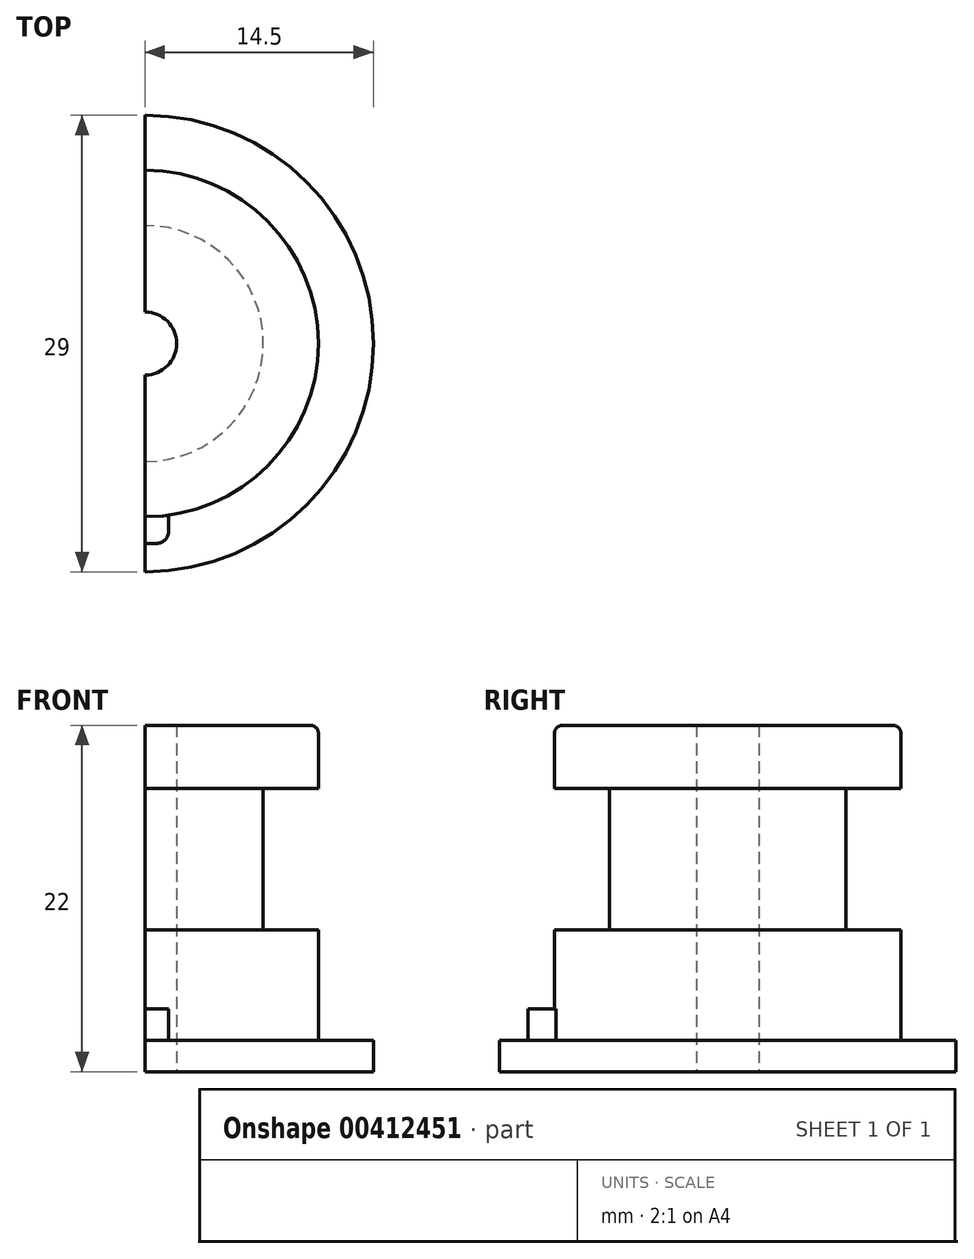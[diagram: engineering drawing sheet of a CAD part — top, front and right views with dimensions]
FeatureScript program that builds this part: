
annotation { "Feature Type Name" : "Feature", "Feature Type Description" : "" }
export const myFeature = defineFeature(function(context is Context, id is Id, definition is map)
    precondition{}
    {
        {
            var Q0;
            Q0=qCreatedBy(makeId("Top.planeOp"),FACE);
            var sketch = newSketch(context, id + "F0", { "sketchPlane" : qUnion([Q0])});
            skCircle(sketch, "E0", {"center": v(0, 0) * mm, "radius": 14.5 * mm});
            skSolve(sketch);
        }
        {
            var Q0;
            Q0=qSketchRegion(id+"F0",true);
            extrude(context, id + "F1", {"entities" : qUnion([Q0]), "depth" : 2 * mm});
        }
        {
            var Q0;
            Q0=makeQuery(id+"F1.opExtrude","CAP_FACE",FACE,{"disambiguationData":[OSD([sQuery(id+"F0.wireOp",EDGE,"E0")])],"isStart":false});
            var sketch = newSketch(context, id + "F2", { "sketchPlane" : qUnion([Q0])});
            skCircle(sketch, "E1", {"center": v(0, 0) * mm, "radius": 11 * mm});
            skSolve(sketch);
        }
        {
            var Q0;
            Q0=qSketchRegion(id+"F2",true);
            extrude(context, id + "F3", {"entities" : qUnion([Q0]), "operationType" : NewBodyOperationType.ADD, "depth" : 20 * mm});
        }
        {
            var Q0;
            Q0=makeQuery(id+"F1.opExtrude","CAP_FACE",FACE,{"disambiguationData":[OSD([sQuery(id+"F0.wireOp",EDGE,"E0")])],"isStart":true});
            var sketch = newSketch(context, id + "F4", { "sketchPlane" : qUnion([Q0])});
            skCircle(sketch, "E2", {"center": v(0, 0) * mm, "radius": 2 * mm});
            skSolve(sketch);
        }
        {
            var Q0;
            Q0=qSketchRegion(id+"F4",true);
            extrude(context, id + "F5", {"entities" : qUnion([Q0]), "operationType" : NewBodyOperationType.REMOVE, "endBound" : BoundingType.THROUGH_ALL, "oppositeDirection" : true, "depth" : 25 * mm});
        }
        {
            var Q0;
            Q0=makeQuery(id+"F1.opExtrude","CAP_FACE",FACE,{"disambiguationData":[OSD([sQuery(id+"F0.wireOp",EDGE,"E0")])],"isStart":false});
            var sketch = newSketch(context, id + "F6", { "sketchPlane" : qUnion([Q0])});
            skLineSegment(sketch, "E3.bottom", {"start": v(-1.5, -9.3) * mm, "end": v(1.5, -9.3) * mm});
            skLineSegment(sketch, "E3.top", {"start": v(-1.5, -12.7) * mm, "end": v(1.5, -12.7) * mm});
            skLineSegment(sketch, "E3.left", {"start": v(-1.5, -9.3) * mm, "end": v(-1.5, -12.7) * mm});
            skLineSegment(sketch, "E3.right", {"start": v(1.5, -9.3) * mm, "end": v(1.5, -12.7) * mm});
            skPoint(sketch, "E3.middle", {"position": v(0, -11) * mm});
            skSolve(sketch);
        }
        {
            var Q0;
            {var subQ0=sQuery(id+"F6.wireOp",EDGE,"E3.top");Q0=makeQuery(id+"F6.imprint","IMPRINT",FACE,{"disambiguationData":[TD([[makeQuery(id+"F6.imprint","IMPRINT",EDGE,{"derivedFrom":subQ0}),1.0]])]});}
            extrude(context, id + "F7", {"entities" : qUnion([Q0]), "operationType" : NewBodyOperationType.ADD, "depth" : 2 * mm});
        }
        {
            var Q0;
            Q0=makeQuery(id+"F7.opExtrude","SWEPT_EDGE",EDGE,{"disambiguationData":[OSD([sQuery(id+"F6.wireOp",EDGE,"E3.top"),sQuery(id+"F6.wireOp",EDGE,"E3.left")])]});
            var Q1;
            Q1=makeQuery(id+"F7.opExtrude","SWEPT_EDGE",EDGE,{"disambiguationData":[OSD([sQuery(id+"F6.wireOp",EDGE,"E3.top"),sQuery(id+"F6.wireOp",EDGE,"E3.right")])]});
            fillet(context, id + "F8", {"entities" : qUnion([Q0, Q1]), "radius" : 0.8 * mm, "tangentPropagation" : true, "allowEdgeOverflow" : false});
        }
        {
            var Q0;
            Q0=makeQuery(id+"F3.opExtrude","CAP_EDGE",EDGE,{"disambiguationData":[OSD([sQuery(id+"F2.wireOp",EDGE,"E1")])],"isStart":false});
            fillet(context, id + "F9", {"entities" : qUnion([Q0]), "radius" : 0.5 * mm, "tangentPropagation" : true, "allowEdgeOverflow" : false});
        }
        {
            var Q0;
            Q0=qCreatedBy(makeId("Front.planeOp"),FACE);
            var sketch = newSketch(context, id + "F10", { "sketchPlane" : qUnion([Q0])});
            skLineSegment(sketch, "E4", {"start": v(11, 2) * mm, "end": v(11, 4.1) * mm});
            skLineSegment(sketch, "E5", {"start": v(11, 4.1) * mm, "end": v(9.18, 3.05) * mm});
            skLineSegment(sketch, "E6", {"start": v(9.18, 3.05) * mm, "end": v(11, 2) * mm});
            skSolve(sketch);
        }
        {
            var Q0;
            Q0=qCreatedBy(makeId("Top.planeOp"),FACE);
            var sketch = newSketch(context, id + "F11", { "sketchPlane" : qUnion([Q0])});
            skLineSegment(sketch, "E7.bottom", {"start": v(0, 29.64) * mm, "end": v(-28.85, 29.64) * mm});
            skLineSegment(sketch, "E7.top", {"start": v(0, -24.5) * mm, "end": v(-28.85, -24.5) * mm});
            skLineSegment(sketch, "E7.left", {"start": v(0, 29.64) * mm, "end": v(0, -24.5) * mm});
            skLineSegment(sketch, "E7.right", {"start": v(-28.85, 29.64) * mm, "end": v(-28.85, -24.5) * mm});
            skSolve(sketch);
        }
        {
            var Q0;
            Q0=qSketchRegion(id+"F11",true);
            extrude(context, id + "F12", {"entities" : qUnion([Q0]), "operationType" : NewBodyOperationType.REMOVE, "endBound" : BoundingType.THROUGH_ALL, "depth" : 25 * mm});
        }
        {
            var Q0;
            Q0=qCreatedBy(makeId("Right.planeOp"),FACE);
            var sketch = newSketch(context, id + "F13", { "sketchPlane" : qUnion([Q0])});
            skLineSegment(sketch, "E8", {"start": v(0, 0) * mm, "end": v(0, 26.62) * mm});
            skSolve(sketch);
        }
        {
            var Q0;
            Q0=qCreatedBy(makeId("Front.planeOp"),FACE);
            var sketch = newSketch(context, id + "F14", { "sketchPlane" : qUnion([Q0])});
            skLineSegment(sketch, "E9.bottom", {"start": v(11, 18) * mm, "end": v(7.5, 18) * mm});
            skLineSegment(sketch, "E9.top", {"start": v(11, 9) * mm, "end": v(7.5, 9) * mm});
            skLineSegment(sketch, "E9.left", {"start": v(11, 18) * mm, "end": v(11, 9) * mm});
            skLineSegment(sketch, "E9.right", {"start": v(7.5, 18) * mm, "end": v(7.5, 9) * mm});
            skSolve(sketch);
        }
        {
            var Q0;
            Q0=qSketchRegion(id+"F14",true);
            var Q1;
            Q1=sQuery(id+"F13.wireOp",EDGE,"E8");
            revolve(context, id + "F15", {"operationType" : NewBodyOperationType.REMOVE, "entities" : qUnion([Q0]), "axis" : qUnion([Q1]), "revolveType" : RevolveType.FULL});
        }
    });
